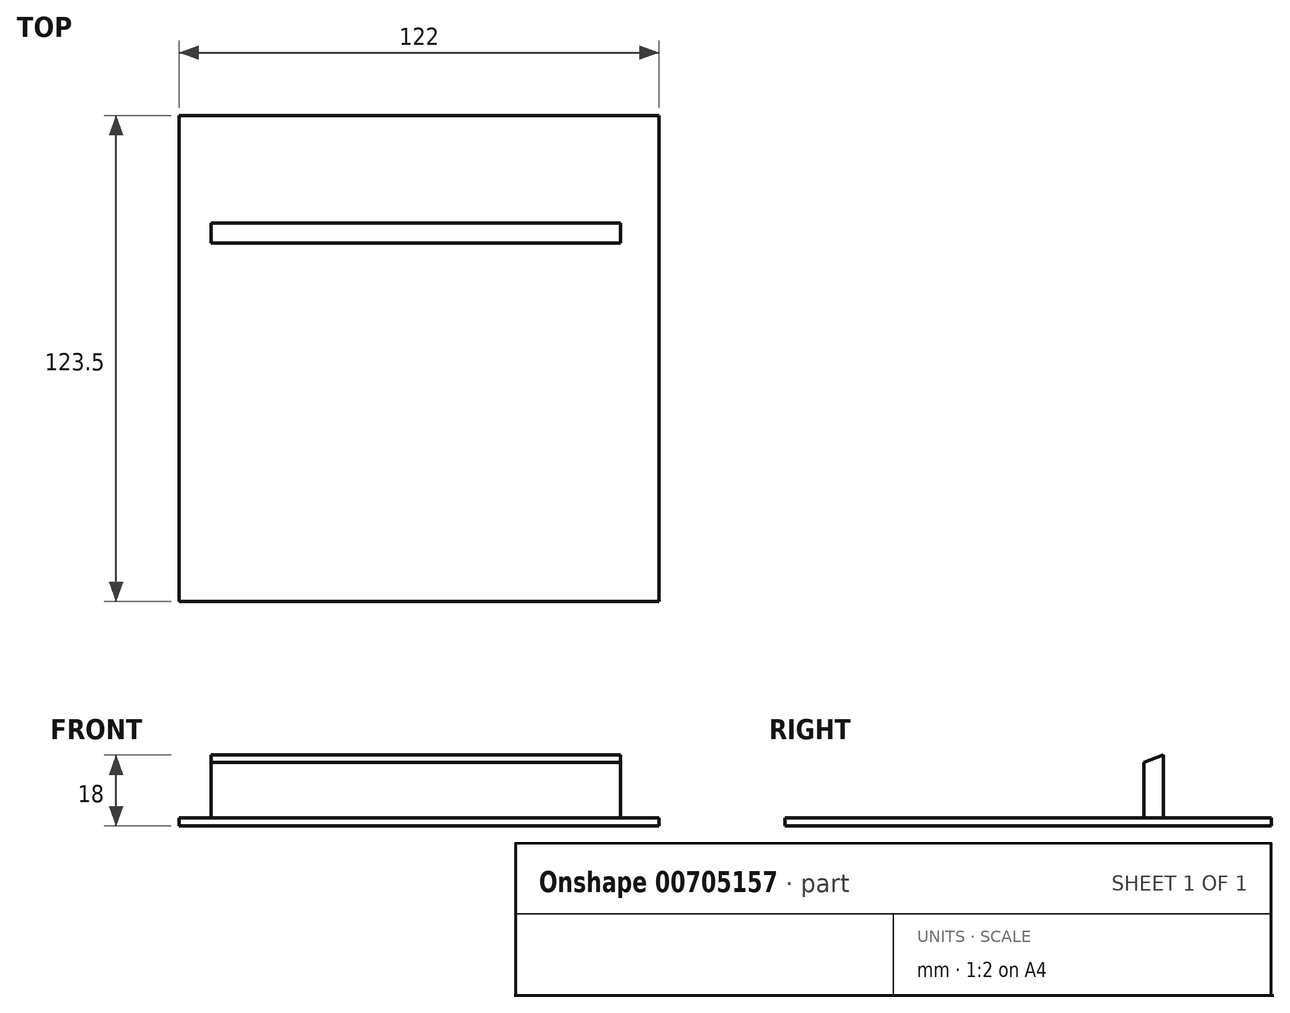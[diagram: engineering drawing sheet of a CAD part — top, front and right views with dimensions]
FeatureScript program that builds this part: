
annotation { "Feature Type Name" : "Feature", "Feature Type Description" : "" }
export const myFeature = defineFeature(function(context is Context, id is Id, definition is map)
    precondition{}
    {
        {
            var Q0;
            Q0=qCreatedBy(makeId("Top.planeOp"),FACE);
            var sketch = newSketch(context, id + "F0", { "sketchPlane" : qUnion([Q0])});
            skLineSegment(sketch, "E0.bottom", {"start": v(-75.63, 48.65) * mm, "end": v(46.37, 48.65) * mm});
            skLineSegment(sketch, "E0.top", {"start": v(-75.63, -74.85) * mm, "end": v(46.37, -74.85) * mm});
            skLineSegment(sketch, "E0.left", {"start": v(-75.63, 48.65) * mm, "end": v(-75.63, -74.85) * mm});
            skLineSegment(sketch, "E0.right", {"start": v(46.37, 48.65) * mm, "end": v(46.37, -74.85) * mm});
            skLineSegment(sketch, "E1.bottom", {"start": v(46.37, 48.65) * mm, "end": v(43.37, 48.65) * mm});
            skLineSegment(sketch, "E1.top", {"start": v(46.37, -74.85) * mm, "end": v(43.37, -74.85) * mm});
            skLineSegment(sketch, "E2.bottom", {"start": v(-75.63, 48.65) * mm, "end": v(-72.63, 48.65) * mm});
            skLineSegment(sketch, "E2.top", {"start": v(-75.63, -74.85) * mm, "end": v(-72.63, -74.85) * mm});
            skLineSegment(sketch, "E3.bottom", {"start": v(43.37, 48.65) * mm, "end": v(-14.63, 48.65) * mm});
            skLineSegment(sketch, "E3.top", {"start": v(43.37, -74.85) * mm, "end": v(-14.63, -74.85) * mm});
            skLineSegment(sketch, "E4.bottom", {"start": v(-14.87, 48.65) * mm, "end": v(-14.37, 48.65) * mm});
            skLineSegment(sketch, "E4.top", {"start": v(-14.87, 18.65) * mm, "end": v(-14.37, 18.65) * mm});
            skLineSegment(sketch, "E5.bottom", {"start": v(-14.37, 48.65) * mm, "end": v(46.37, 48.65) * mm});
            skLineSegment(sketch, "E5.top", {"start": v(-14.37, -74.85) * mm, "end": v(46.37, -74.85) * mm});
            skLineSegment(sketch, "E6.bottom", {"start": v(-67.42, 21.29) * mm, "end": v(36.6, 21.29) * mm});
            skLineSegment(sketch, "E6.top", {"start": v(-67.42, 16.29) * mm, "end": v(36.6, 16.29) * mm});
            skLineSegment(sketch, "E6.left", {"start": v(-67.42, 21.29) * mm, "end": v(-67.42, 16.29) * mm});
            skLineSegment(sketch, "E6.right", {"start": v(36.6, 21.29) * mm, "end": v(36.6, 16.29) * mm});
            skSolve(sketch);
        }
        {
            var Q0;
            Q0 = qSketchRegion(id + "F0", true);
            var Q1;
            Q1=makeQuery(id+"F0.imprint","IMPRINT",FACE,{"disambiguationData":[TD([[makeQuery(id+"F0.imprint","IMPRINT",EDGE,{"derivedFrom":sQuery(id+"F0.wireOp",EDGE,"E6.bottom")}),-1.0]])]});
            extrude(context, id + "F1", {"entities" : qUnion([Q0, Q1]), "oppositeDirection" : true, "depth" : 2 * mm, "offsetDistance" : 25 * mm});
        }
        {
            var Q0;
            Q0=makeQuery(id+"F0.imprint","IMPRINT",FACE,{"disambiguationData":[TD([[makeQuery(id+"F0.imprint","IMPRINT",EDGE,{"derivedFrom":sQuery(id+"F0.wireOp",EDGE,"E6.bottom")}),-1.0]])]});
            extrude(context, id + "F2", {"entities" : qUnion([Q0]), "operationType" : NewBodyOperationType.ADD, "depth" : 16 * mm, "offsetDistance" : 25 * mm});
        }
        {
            var Q0;
            Q0=makeQuery(id+"F2.opExtrude","CAP_EDGE",EDGE,{"disambiguationData":[OSD([sQuery(id+"F0.wireOp",EDGE,"E6.top")])],"isStart":false});
            chamfer(context, id + "F3", {"entities" : qUnion([Q0]), "chamferType" : ChamferType.OFFSET_ANGLE, "width" : 5 * mm, "oppositeDirection" : false, "angle" : 20 * degree, "tangentPropagation" : true});
        }
    });
